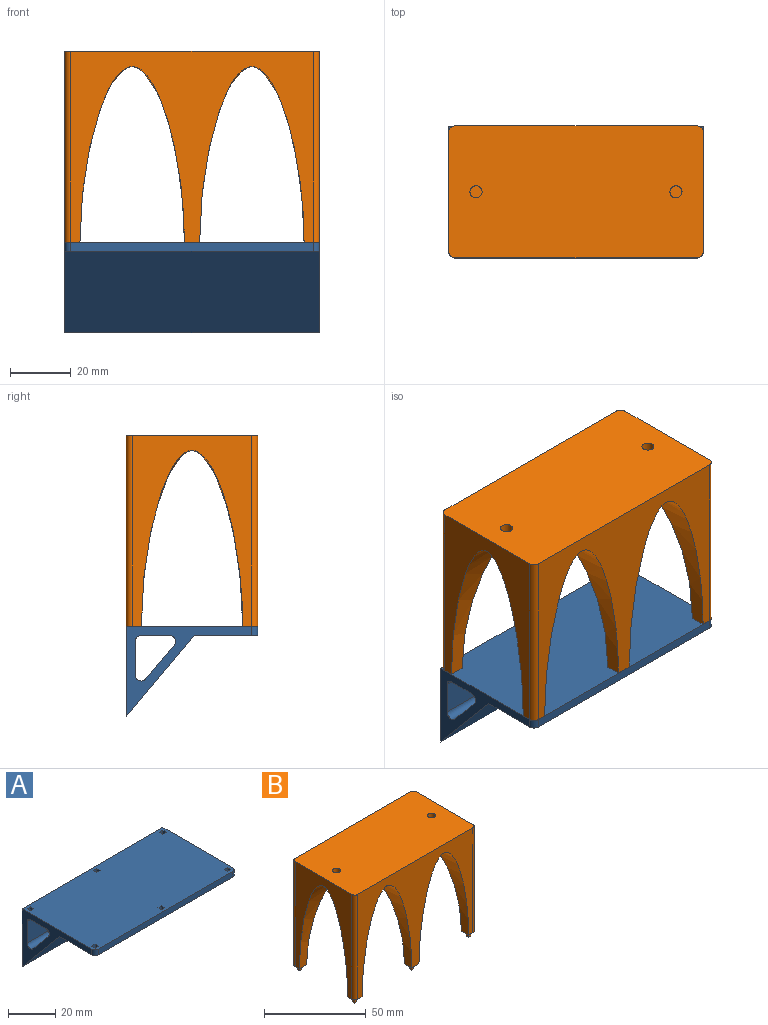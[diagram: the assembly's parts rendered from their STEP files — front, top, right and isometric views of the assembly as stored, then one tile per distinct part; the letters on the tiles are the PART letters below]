
ASSEMBLY  parts=2 mates=1
PART A: 42 faces, bbox 84x43.5x29.8 mm
  f0: plane 84x43.5mm, normal (0,0,1), area 3628.1mm2, adj f3,f8,f9,f10,f11,f12,f15,f16
  f1: plane 84x21mm, normal (0,0,-1), area 1750.3mm2, adj f3,f4,f9,f10,f11,f12,f30,f31
  f2: cylinder r=2mm len=84mm, axis (1,0,0), area 261.5mm2, adj f6,f7,f9,f10,f15,f16,f17,f18
  f3: plane 80x3mm, normal (0,-1,0), area 240mm2, adj f0,f1,f11,f12
  f4: plane 84x26.81mm, normal (0,-0.77,-0.64), area 2940mm2, adj f1,f8,f9,f10
  f5: plane 84x11.07mm, normal (0,0.77,0.64), area 1214.3mm2, adj f9,f10,f13,f14
  f6: plane 84x9.29mm, normal (0,0,-1), area 780.6mm2, adj f2,f9,f10,f13
  f7: plane 84x11.07mm, normal (0,-1,0), area 930.2mm2, adj f2,f9,f10,f14
  f8: plane 84x29.81mm, normal (0,1,0), area 2504.2mm2, adj f0,f4,f9,f10
  f9: plane 41.5x29.81mm, normal (-1,0,0), area 292.4mm2, adj f0,f1,f2,f4,f5,f6,f7,f8
  f10: plane 41.5x29.81mm, normal (1,0,0), area 292.4mm2, adj f0,f1,f2,f4,f5,f6,f7,f8
  f11: cylinder r=2mm len=3mm, axis (0,0,-1), area 9.4mm2, adj f0,f1,f3,f10
  f12: cylinder r=2mm len=3mm, axis (0,0,1), area 9.4mm2, adj f0,f1,f3,f9
  f13: cylinder r=2mm len=84mm, axis (1,0,0), area 381.2mm2, adj f5,f6,f9,f10
  f14: cylinder r=2mm len=84mm, axis (-1,0,0), area 410.5mm2, adj f5,f7,f9,f10
  f15: plane 3.68x2mm, normal (0,1,0), area 7.4mm2, adj f0,f2,f16,f17
  f16: plane 4x2mm, normal (-1,0,0), area 8mm2, adj f0,f2,f15,f18,f19
  f17: plane 4x2mm, normal (1,0,0), area 8mm2, adj f0,f2,f15,f18,f19
  f18: plane 2x1.77mm, normal (0,0,1), area 3.5mm2, adj f2,f16,f17,f19
  f19: plane 4x2mm, normal (0,-1,0), area 8mm2, adj f0,f16,f17,f18
  f20: plane 3.68x2mm, normal (0,1,0), area 7.4mm2, adj f0,f2,f21,f22
  f21: plane 4x2mm, normal (-1,0,0), area 8mm2, adj f0,f2,f20,f23,f24
  f22: plane 4x2mm, normal (1,0,0), area 8mm2, adj f0,f2,f20,f23,f24
  f23: plane 2x1.77mm, normal (0,0,1), area 3.5mm2, adj f2,f21,f22,f24
  f24: plane 4x2mm, normal (0,-1,0), area 8mm2, adj f0,f21,f22,f23
  f25: plane 4x2mm, normal (-1,0,0), area 8mm2, adj f0,f2,f27,f28,f29
  f26: plane 4x2mm, normal (1,0,0), area 8mm2, adj f0,f2,f27,f28,f29
  f27: plane 3.68x2mm, normal (0,1,0), area 7.4mm2, adj f0,f2,f25,f26
  f28: plane 2x1.77mm, normal (0,0,1), area 3.5mm2, adj f2,f25,f26,f29
  f29: plane 4x2mm, normal (0,-1,0), area 8mm2, adj f0,f25,f26,f28
  f30: plane 3x2mm, normal (0,1,0), area 6mm2, adj f0,f1,f31,f33
  f31: plane 3x2mm, normal (-1,0,0), area 6mm2, adj f0,f1,f30,f32
  f32: plane 3x2mm, normal (0,-1,0), area 6mm2, adj f0,f1,f31,f33
  f33: plane 3x2mm, normal (1,0,0), area 6mm2, adj f0,f1,f30,f32
  f34: plane 3x2mm, normal (0,1,0), area 6mm2, adj f0,f1,f35,f37
  f35: plane 3x2mm, normal (-1,0,0), area 6mm2, adj f0,f1,f34,f36
  f36: plane 3x2mm, normal (0,-1,0), area 6mm2, adj f0,f1,f35,f37
  f37: plane 3x2mm, normal (1,0,0), area 6mm2, adj f0,f1,f34,f36
  f38: plane 3x2mm, normal (0,1,0), area 6mm2, adj f0,f1,f39,f41
  f39: plane 3x2mm, normal (-1,0,0), area 6mm2, adj f0,f1,f38,f40
  f40: plane 3x2mm, normal (0,-1,0), area 6mm2, adj f0,f1,f39,f41
  f41: plane 3x2mm, normal (1,0,0), area 6mm2, adj f0,f1,f38,f40
PART B: 56 faces, bbox 84x43.5x66 mm
  f0: plane 5x5mm, normal (0,0,-1), area 21.9mm2, adj f7,f8,f9,f14,f18,f31,f32,f33
  f1: plane 5x5mm, normal (0,0,-1), area 21.9mm2, adj f5,f9,f13,f16,f20,f51,f52,f53
  f2: plane 5x5mm, normal (0,0,-1), area 22.7mm2, adj f6,f9,f14,f16,f26,f27,f28,f29
  f3: plane 5x5mm, normal (0,0,-1), area 21.9mm2, adj f5,f11,f13,f17,f21,f46,f47,f48
  f4: plane 5x5mm, normal (0,0,-1), area 22.7mm2, adj f6,f11,f15,f17,f41,f42,f43,f44
  f5: extruded ~58x33.5mm, area 1221.1mm2, adj f1,f3,f13,f16,f17
  f6: extruded ~58x39.5mm, area 1813.9mm2, adj f2,f4,f14,f15,f16,f17
  f7: extruded ~58x33.5mm, area 1221mm2, adj f0,f8,f10,f14,f15
  f8: plane 63x39.5mm, normal (1,0,0), area 1006.9mm2, adj f0,f7,f10,f12,f18,f19
  f9: plane 80x63mm, normal (0,-1,0), area 1988.5mm2, adj f0,f1,f2,f12,f14,f16,f18,f20
  f10: plane 5x5mm, normal (0,0,-1), area 21.9mm2, adj f7,f8,f11,f15,f19,f36,f37,f38
  f11: plane 80x63mm, normal (0,1,0), area 1988.5mm2, adj f3,f4,f10,f12,f15,f17,f19,f21
  f12: plane 84x43.5mm, normal (0,0,1), area 3625.4mm2, adj f8,f9,f11,f13,f18,f19,f20,f21
  f13: plane 63x39.5mm, normal (-1,0,0), area 1006.9mm2, adj f1,f3,f5,f12,f20,f21
  f14: extruded ~58x34.5mm, area 1211.4mm2, adj f0,f2,f6,f7,f9
  f15: extruded ~58x34.5mm, area 1211.4mm2, adj f4,f6,f7,f10,f11
  f16: extruded ~58x34.5mm, area 1211.4mm2, adj f1,f2,f5,f6,f9
  f17: extruded ~58x34.5mm, area 1211.4mm2, adj f3,f4,f5,f6,f11
  f18: cylinder r=2mm len=63mm, axis (0,0,-1), area 197.9mm2, adj f0,f8,f9,f12
  f19: cylinder r=2mm len=63mm, axis (0,0,1), area 197.9mm2, adj f8,f10,f11,f12
  f20: cylinder r=2mm len=63mm, axis (0,0,1), area 197.9mm2, adj f1,f9,f12,f13
  f21: cylinder r=2mm len=63mm, axis (0,0,-1), area 197.9mm2, adj f3,f11,f12,f13
  f22: cylinder r=2mm len=4mm, axis (0,0,1), area 50.3mm2, adj f12,f23
  f23: plane 4x4mm, normal (0,0,1), area 12.6mm2, adj f22
  f24: cylinder r=2mm len=4mm, axis (0,0,1), area 50.3mm2, adj f12,f25
  f25: plane 4x4mm, normal (0,0,1), area 12.6mm2, adj f24
  f26: plane 3x1.5mm, normal (0,1,0), area 4.5mm2, adj f2,f27,f29,f30
  f27: plane 3x1.5mm, normal (1,0,0), area 4.5mm2, adj f2,f26,f28,f30
  f28: plane 3x1.5mm, normal (0,-1,0), area 4.5mm2, adj f2,f27,f29,f30
  f29: plane 3x1.5mm, normal (-1,0,0), area 4.5mm2, adj f2,f26,f28,f30
  f30: plane 1.5x1.5mm, normal (0,0,-1), area 2.3mm2, adj f26,f27,f28,f29
  f31: plane 3x1.5mm, normal (1,0,0), area 4.5mm2, adj f0,f32,f34,f35
  f32: plane 3x1.5mm, normal (0,-1,0), area 4.5mm2, adj f0,f31,f33,f35
  f33: plane 3x1.5mm, normal (-1,0,0), area 4.5mm2, adj f0,f32,f34,f35
  f34: plane 3x1.5mm, normal (0,1,0), area 4.5mm2, adj f0,f31,f33,f35
  f35: plane 1.5x1.5mm, normal (0,0,-1), area 2.3mm2, adj f31,f32,f33,f34
  f36: plane 3x1.5mm, normal (0,1,0), area 4.5mm2, adj f10,f37,f39,f40
  f37: plane 3x1.5mm, normal (1,0,0), area 4.5mm2, adj f10,f36,f38,f40
  f38: plane 3x1.5mm, normal (0,-1,0), area 4.5mm2, adj f10,f37,f39,f40
  f39: plane 3x1.5mm, normal (-1,0,0), area 4.5mm2, adj f10,f36,f38,f40
  f40: plane 1.5x1.5mm, normal (0,0,-1), area 2.3mm2, adj f36,f37,f38,f39
  f41: plane 3x1.5mm, normal (0,1,0), area 4.5mm2, adj f4,f42,f44,f45
  f42: plane 3x1.5mm, normal (1,0,0), area 4.5mm2, adj f4,f41,f43,f45
  f43: plane 3x1.5mm, normal (0,-1,0), area 4.5mm2, adj f4,f42,f44,f45
  f44: plane 3x1.5mm, normal (-1,0,0), area 4.5mm2, adj f4,f41,f43,f45
  f45: plane 1.5x1.5mm, normal (0,0,-1), area 2.3mm2, adj f41,f42,f43,f44
  f46: plane 3x1.5mm, normal (0,1,0), area 4.5mm2, adj f3,f47,f49,f50
  f47: plane 3x1.5mm, normal (1,0,0), area 4.5mm2, adj f3,f46,f48,f50
  f48: plane 3x1.5mm, normal (0,-1,0), area 4.5mm2, adj f3,f47,f49,f50
  f49: plane 3x1.5mm, normal (-1,0,0), area 4.5mm2, adj f3,f46,f48,f50
  f50: plane 1.5x1.5mm, normal (0,0,-1), area 2.3mm2, adj f46,f47,f48,f49
  f51: plane 3x1.5mm, normal (0,1,0), area 4.5mm2, adj f1,f52,f54,f55
  f52: plane 3x1.5mm, normal (1,0,0), area 4.5mm2, adj f1,f51,f53,f55
  f53: plane 3x1.5mm, normal (0,-1,0), area 4.5mm2, adj f1,f52,f54,f55
  f54: plane 3x1.5mm, normal (-1,0,0), area 4.5mm2, adj f1,f51,f53,f55
  f55: plane 1.5x1.5mm, normal (0,0,-1), area 2.3mm2, adj f51,f52,f53,f54
PLACE A t=(-2.69,-31.47,-8.87)mm
PLACE B t=(-2.69,-31.47,-8.87)mm
MATE fastened B.f18 <-> A.f11  axis (0,0,-1) through (-4.69,-29.47,-5.87)mm
